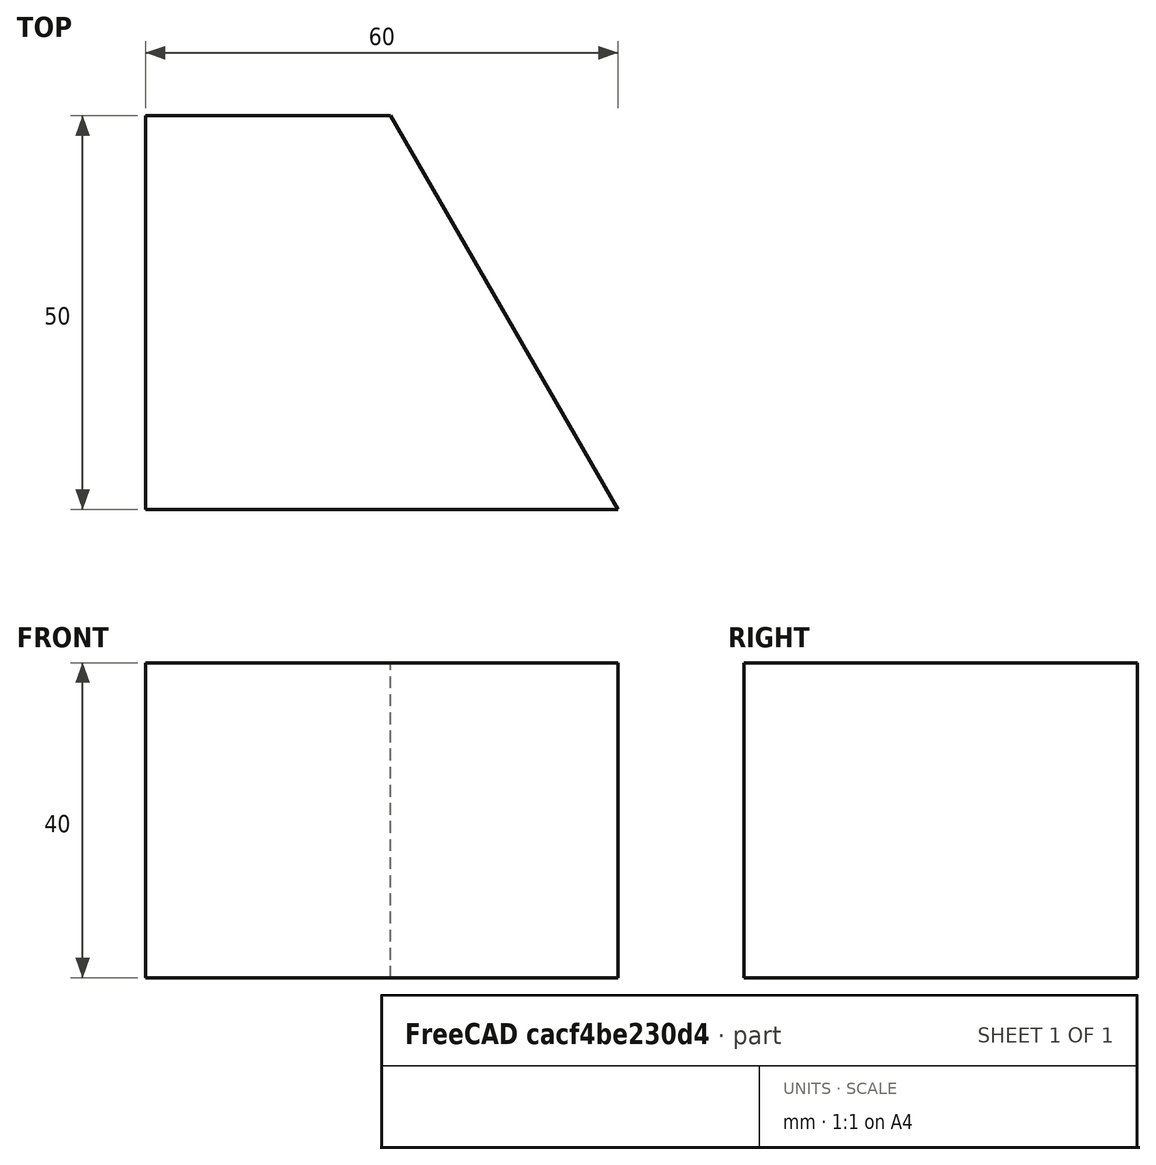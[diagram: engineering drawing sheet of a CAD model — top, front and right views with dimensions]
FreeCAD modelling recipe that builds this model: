
FCSTD DOCUMENT  (FreeCAD 0.19R)
Label: Trapezium
License: All rights reserved
LicenseURL: http://en.wikipedia.org/wiki/All_rights_reserved
objects: Sketcher::SketchObject×1, PartDesign::Pad×1, PartDesign::Body×1
note: 4 computed .brp shape members not serialized (recipe doc carries the construction recipe); baked Part::Feature solids carry a one-line shape summary decoded from their .brp

FEATURE [Sketcher::SketchObject] Sketch
  FullyConstrained = true
  MapMode = 5
  Support = -> [XY_Plane]
  sketch-geometry (4):
    g0: LineSegment StartX=8 StartY=58 StartZ=0 EndX=39.1325 EndY=58 EndZ=0
    g1: LineSegment StartX=39.1325 StartY=58 StartZ=0 EndX=68 EndY=8 EndZ=0
    g2: LineSegment StartX=68 StartY=8 StartZ=0 EndX=8 EndY=8 EndZ=0
    g3: LineSegment StartX=8 StartY=8 StartZ=0 EndX=8 EndY=58 EndZ=0
  constraints (12):
    c: Coincident(g0,g1)
    c: Coincident(g1,g2)
    c: Coincident(g2,g3)
    c: Coincident(g3,g0)
    c: Horizontal(g0)
    c: Horizontal(g2)
    c: Vertical(g3)
    c: DistanceX(g-1,g2) = 8
    c: DistanceY(g-1,g2) = 8
    c: DistanceY(g2,g0) = 50
    c: DistanceX(g2,g1) = 60
    c: Angle(g1,g2) = 1.0472
FEATURE [PartDesign::Pad] Pad
  Direction = (1,1,1)
  Length = 40
  Length2 = 100
  Profile = -> Sketch
  Type = 0
FEATURE [PartDesign::Body] Body
  Group = -> [Sketch,Pad]
  Origin = -> Origin
  Tip = -> Pad
